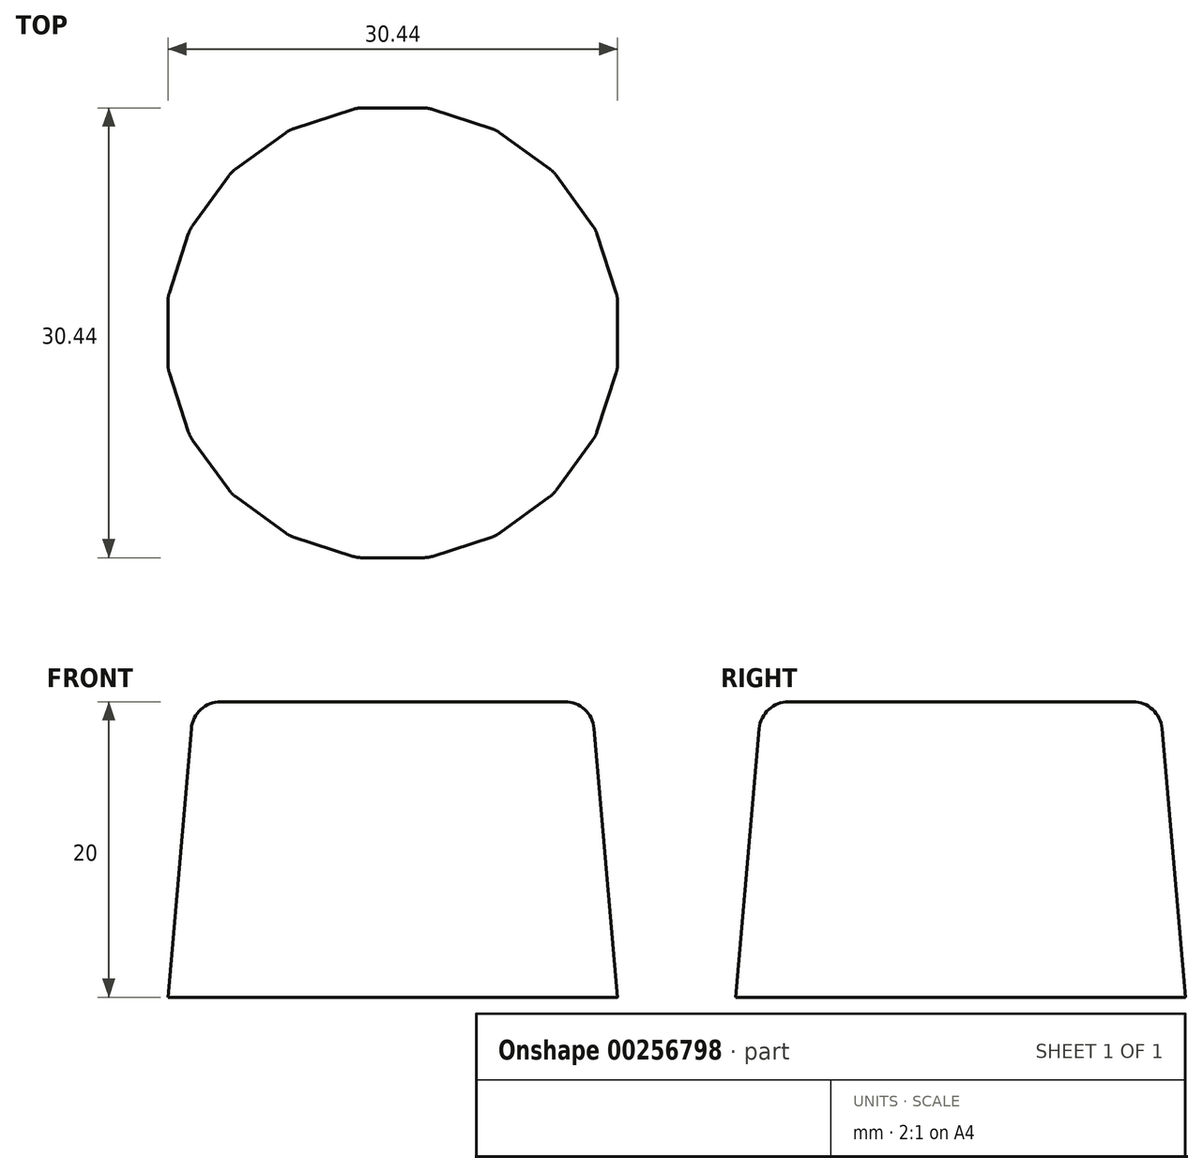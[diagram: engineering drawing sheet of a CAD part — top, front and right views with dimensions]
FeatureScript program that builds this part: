
annotation { "Feature Type Name" : "Feature", "Feature Type Description" : "" }
export const myFeature = defineFeature(function(context is Context, id is Id, definition is map)
    precondition{}
    {
        {
            var Q0;
            Q0=qCreatedBy(makeId("Top.planeOp"),FACE);
            var sketch = newSketch(context, id + "F0", { "sketchPlane" : qUnion([Q0])});
            skCircle(sketch, "E0.cCircle", {"center": v(0, 0) * mm, "radius": 15.22 * mm, "construction": true});
            skLineSegment(sketch, "E0.0", {"start": v(15.22, 2.41) * mm, "end": v(15.22, -2.41) * mm});
            skLineSegment(sketch, "E0.1", {"start": v(15.22, -2.41) * mm, "end": v(13.73, -7) * mm});
            skLineSegment(sketch, "E0.2", {"start": v(13.73, -7) * mm, "end": v(10.9, -10.9) * mm});
            skLineSegment(sketch, "E0.3", {"start": v(10.9, -10.9) * mm, "end": v(7, -13.73) * mm});
            skLineSegment(sketch, "E0.4", {"start": v(7, -13.73) * mm, "end": v(2.41, -15.22) * mm});
            skLineSegment(sketch, "E0.5", {"start": v(2.41, -15.22) * mm, "end": v(-2.41, -15.22) * mm});
            skLineSegment(sketch, "E0.6", {"start": v(-2.41, -15.22) * mm, "end": v(-7, -13.73) * mm});
            skLineSegment(sketch, "E0.7", {"start": v(-7, -13.73) * mm, "end": v(-10.9, -10.9) * mm});
            skLineSegment(sketch, "E0.8", {"start": v(-10.9, -10.9) * mm, "end": v(-13.73, -7) * mm});
            skLineSegment(sketch, "E0.9", {"start": v(-13.73, -7) * mm, "end": v(-15.22, -2.41) * mm});
            skLineSegment(sketch, "E0.10", {"start": v(-15.22, -2.41) * mm, "end": v(-15.22, 2.41) * mm});
            skLineSegment(sketch, "E0.11", {"start": v(-15.22, 2.41) * mm, "end": v(-13.73, 7) * mm});
            skLineSegment(sketch, "E0.12", {"start": v(-13.73, 7) * mm, "end": v(-10.9, 10.9) * mm});
            skLineSegment(sketch, "E0.13", {"start": v(-10.9, 10.9) * mm, "end": v(-7, 13.73) * mm});
            skLineSegment(sketch, "E0.14", {"start": v(-7, 13.73) * mm, "end": v(-2.41, 15.22) * mm});
            skLineSegment(sketch, "E0.15", {"start": v(-2.41, 15.22) * mm, "end": v(2.41, 15.22) * mm});
            skLineSegment(sketch, "E0.16", {"start": v(2.41, 15.22) * mm, "end": v(7, 13.73) * mm});
            skLineSegment(sketch, "E0.17", {"start": v(7, 13.73) * mm, "end": v(10.9, 10.9) * mm});
            skLineSegment(sketch, "E0.18", {"start": v(10.9, 10.9) * mm, "end": v(13.73, 7) * mm});
            skLineSegment(sketch, "E0.19", {"start": v(13.73, 7) * mm, "end": v(15.22, 2.41) * mm});
            skPoint(sketch, "E0.0.midPoint", {"position": v(15.22, 0) * mm});
            skSolve(sketch);
        }
        {
            var Q0;
            Q0=qSketchRegion(id+"F0",true);
            extrude(context, id + "F1", {"entities" : qUnion([Q0]), "depth" : 20 * mm, "hasDraft" : true, "draftAngle" : 5 * degree, "draftPullDirection" : true});
        }
        {
            var Q0;
            Q0=makeQuery(id+"F1.opExtrude","CAP_EDGE",EDGE,{"disambiguationData":[OSD([sQuery(id+"F0.wireOp",EDGE,"E0.15")])],"isStart":false});
            var Q1;
            Q1=makeQuery(id+"F1.opExtrude","CAP_EDGE",EDGE,{"disambiguationData":[OSD([sQuery(id+"F0.wireOp",EDGE,"E0.16")])],"isStart":false});
            var Q2;
            Q2=makeQuery(id+"F1.opExtrude","CAP_EDGE",EDGE,{"disambiguationData":[OSD([sQuery(id+"F0.wireOp",EDGE,"E0.17")])],"isStart":false});
            var Q3;
            Q3=makeQuery(id+"F1.opExtrude","CAP_EDGE",EDGE,{"disambiguationData":[OSD([sQuery(id+"F0.wireOp",EDGE,"E0.12")])],"isStart":false});
            var Q4;
            Q4=makeQuery(id+"F1.opExtrude","CAP_FACE",FACE,{"disambiguationData":[OSD([sQuery(id+"F0.wireOp",EDGE,"E0.0"),sQuery(id+"F0.wireOp",EDGE,"E0.1"),sQuery(id+"F0.wireOp",EDGE,"E0.2"),sQuery(id+"F0.wireOp",EDGE,"E0.3"),sQuery(id+"F0.wireOp",EDGE,"E0.4"),sQuery(id+"F0.wireOp",EDGE,"E0.5"),sQuery(id+"F0.wireOp",EDGE,"E0.6"),sQuery(id+"F0.wireOp",EDGE,"E0.7"),sQuery(id+"F0.wireOp",EDGE,"E0.8"),sQuery(id+"F0.wireOp",EDGE,"E0.9"),sQuery(id+"F0.wireOp",EDGE,"E0.10"),sQuery(id+"F0.wireOp",EDGE,"E0.11"),sQuery(id+"F0.wireOp",EDGE,"E0.12"),sQuery(id+"F0.wireOp",EDGE,"E0.13"),sQuery(id+"F0.wireOp",EDGE,"E0.14"),sQuery(id+"F0.wireOp",EDGE,"E0.15"),sQuery(id+"F0.wireOp",EDGE,"E0.16"),sQuery(id+"F0.wireOp",EDGE,"E0.17"),sQuery(id+"F0.wireOp",EDGE,"E0.18"),sQuery(id+"F0.wireOp",EDGE,"E0.19")])],"isStart":false});
            var Q5;
            Q5=makeQuery(id+"F1.opExtrude","SWEPT_EDGE",EDGE,{"disambiguationData":[OSD([sQuery(id+"F0.wireOp",EDGE,"E0.15"),sQuery(id+"F0.wireOp",EDGE,"E0.16")])]});
            var Q6;
            Q6=makeQuery(id+"F1.opExtrude","SWEPT_EDGE",EDGE,{"disambiguationData":[OSD([sQuery(id+"F0.wireOp",EDGE,"E0.14"),sQuery(id+"F0.wireOp",EDGE,"E0.15")])]});
            var Q7;
            Q7=makeQuery(id+"F1.opExtrude","SWEPT_EDGE",EDGE,{"disambiguationData":[OSD([sQuery(id+"F0.wireOp",EDGE,"E0.13"),sQuery(id+"F0.wireOp",EDGE,"E0.14")])]});
            var Q8;
            Q8=makeQuery(id+"F1.opExtrude","SWEPT_EDGE",EDGE,{"disambiguationData":[OSD([sQuery(id+"F0.wireOp",EDGE,"E0.12"),sQuery(id+"F0.wireOp",EDGE,"E0.13")])]});
            var Q9;
            Q9=makeQuery(id+"F1.opExtrude","SWEPT_EDGE",EDGE,{"disambiguationData":[OSD([sQuery(id+"F0.wireOp",EDGE,"E0.11"),sQuery(id+"F0.wireOp",EDGE,"E0.12")])]});
            var Q10;
            Q10=makeQuery(id+"F1.opExtrude","SWEPT_EDGE",EDGE,{"disambiguationData":[OSD([sQuery(id+"F0.wireOp",EDGE,"E0.10"),sQuery(id+"F0.wireOp",EDGE,"E0.11")])]});
            var Q11;
            Q11=makeQuery(id+"F1.opExtrude","SWEPT_EDGE",EDGE,{"disambiguationData":[OSD([sQuery(id+"F0.wireOp",EDGE,"E0.9"),sQuery(id+"F0.wireOp",EDGE,"E0.10")])]});
            var Q12;
            Q12=makeQuery(id+"F1.opExtrude","SWEPT_EDGE",EDGE,{"disambiguationData":[OSD([sQuery(id+"F0.wireOp",EDGE,"E0.8"),sQuery(id+"F0.wireOp",EDGE,"E0.9")])]});
            var Q13;
            Q13=makeQuery(id+"F1.opExtrude","SWEPT_EDGE",EDGE,{"disambiguationData":[OSD([sQuery(id+"F0.wireOp",EDGE,"E0.7"),sQuery(id+"F0.wireOp",EDGE,"E0.8")])]});
            var Q14;
            Q14=makeQuery(id+"F1.opExtrude","SWEPT_EDGE",EDGE,{"disambiguationData":[OSD([sQuery(id+"F0.wireOp",EDGE,"E0.6"),sQuery(id+"F0.wireOp",EDGE,"E0.7")])]});
            var Q15;
            Q15=makeQuery(id+"F1.opExtrude","SWEPT_EDGE",EDGE,{"disambiguationData":[OSD([sQuery(id+"F0.wireOp",EDGE,"E0.5"),sQuery(id+"F0.wireOp",EDGE,"E0.6")])]});
            var Q16;
            Q16=makeQuery(id+"F1.opExtrude","SWEPT_EDGE",EDGE,{"disambiguationData":[OSD([sQuery(id+"F0.wireOp",EDGE,"E0.4"),sQuery(id+"F0.wireOp",EDGE,"E0.5")])]});
            var Q17;
            Q17=makeQuery(id+"F1.opExtrude","SWEPT_EDGE",EDGE,{"disambiguationData":[OSD([sQuery(id+"F0.wireOp",EDGE,"E0.3"),sQuery(id+"F0.wireOp",EDGE,"E0.4")])]});
            var Q18;
            Q18=makeQuery(id+"F1.opExtrude","SWEPT_EDGE",EDGE,{"disambiguationData":[OSD([sQuery(id+"F0.wireOp",EDGE,"E0.2"),sQuery(id+"F0.wireOp",EDGE,"E0.3")])]});
            var Q19;
            Q19=makeQuery(id+"F1.opExtrude","SWEPT_EDGE",EDGE,{"disambiguationData":[OSD([sQuery(id+"F0.wireOp",EDGE,"E0.18"),sQuery(id+"F0.wireOp",EDGE,"E0.19")])]});
            var Q20;
            Q20=makeQuery(id+"F1.opExtrude","SWEPT_EDGE",EDGE,{"disambiguationData":[OSD([sQuery(id+"F0.wireOp",EDGE,"E0.16"),sQuery(id+"F0.wireOp",EDGE,"E0.17")])]});
            var Q21;
            Q21=makeQuery(id+"F1.opExtrude","SWEPT_EDGE",EDGE,{"disambiguationData":[OSD([sQuery(id+"F0.wireOp",EDGE,"E0.17"),sQuery(id+"F0.wireOp",EDGE,"E0.18")])]});
            var Q22;
            Q22=makeQuery(id+"F1.opExtrude","SWEPT_EDGE",EDGE,{"disambiguationData":[OSD([sQuery(id+"F0.wireOp",EDGE,"E0.0"),sQuery(id+"F0.wireOp",EDGE,"E0.19")])]});
            var Q23;
            Q23=makeQuery(id+"F1.opExtrude","SWEPT_EDGE",EDGE,{"disambiguationData":[OSD([sQuery(id+"F0.wireOp",EDGE,"E0.0"),sQuery(id+"F0.wireOp",EDGE,"E0.1")])]});
            var Q24;
            Q24=makeQuery(id+"F1.opExtrude","SWEPT_EDGE",EDGE,{"disambiguationData":[OSD([sQuery(id+"F0.wireOp",EDGE,"E0.1"),sQuery(id+"F0.wireOp",EDGE,"E0.2")])]});
            fillet(context, id + "F2", {"entities" : qUnion([Q0, Q1, Q2, Q3, Q4, Q5, Q6, Q7, Q8, Q9, Q10, Q11, Q12, Q13, Q14, Q15, Q16, Q17, Q18, Q19, Q20, Q21, Q22, Q23, Q24]), "radius" : 2 * mm, "tangentPropagation" : true, "allowEdgeOverflow" : false});
        }
    });
